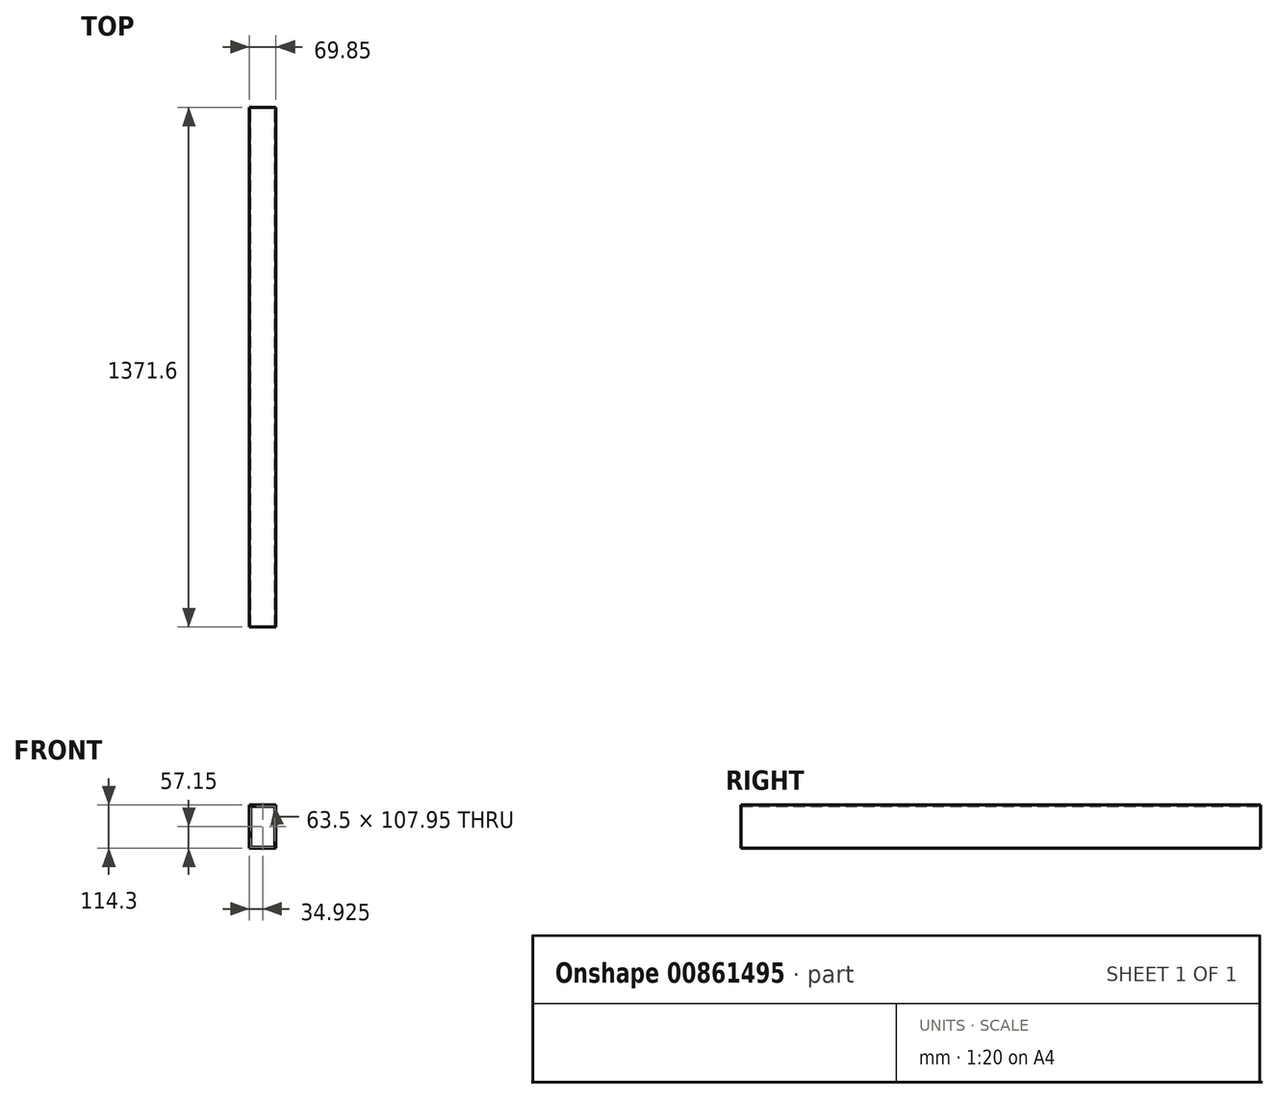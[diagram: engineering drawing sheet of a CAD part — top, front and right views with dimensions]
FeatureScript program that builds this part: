
annotation { "Feature Type Name" : "Feature", "Feature Type Description" : "" }
export const myFeature = defineFeature(function(context is Context, id is Id, definition is map)
    precondition{}
    {
        {
            var Q0;
            Q0=qCreatedBy(makeId("Front.planeOp"),FACE);
            var sketch = newSketch(context, id + "F0", { "sketchPlane" : qUnion([Q0])});
            skLineSegment(sketch, "E0.bottom", {"start": v(0, 0) * mm, "end": v(69.85, 0) * mm});
            skLineSegment(sketch, "E0.top", {"start": v(0, 114.3) * mm, "end": v(69.85, 114.3) * mm});
            skLineSegment(sketch, "E0.left", {"start": v(0, 0) * mm, "end": v(0, 114.3) * mm});
            skLineSegment(sketch, "E0.right", {"start": v(69.85, 0) * mm, "end": v(69.85, 114.3) * mm});
            skLineSegment(sketch, "E1.bottom", {"start": v(3.17, 3.18) * mm, "end": v(66.68, 3.18) * mm});
            skLineSegment(sketch, "E1.top", {"start": v(3.17, 111.13) * mm, "end": v(66.67, 111.13) * mm});
            skLineSegment(sketch, "E1.left", {"start": v(3.17, 3.17) * mm, "end": v(3.17, 111.13) * mm});
            skLineSegment(sketch, "E1.right", {"start": v(66.68, 3.17) * mm, "end": v(66.67, 111.13) * mm});
            skSolve(sketch);
        }
        {
            var Q0;
            Q0=makeQuery(id+"F0.imprint","IMPRINT",FACE,{"disambiguationData":[TD([[makeQuery(id+"F0.imprint","IMPRINT",EDGE,{"derivedFrom":sQuery(id+"F0.wireOp",EDGE,"E0.bottom")}),1.0]])]});
            extrude(context, id + "F1", {"entities" : qUnion([Q0]), "depth" : 1371.6 * mm, "offsetDistance" : 25.4 * mm});
        }
    });
